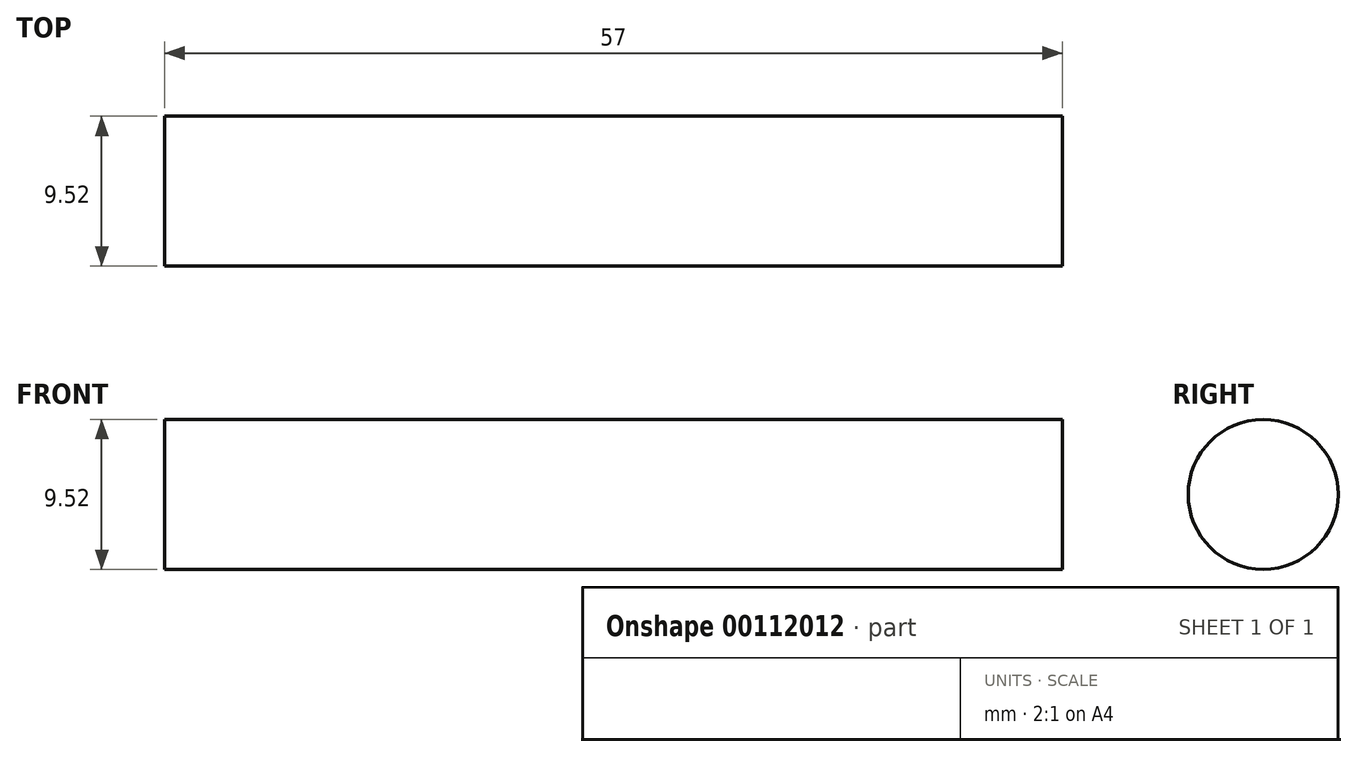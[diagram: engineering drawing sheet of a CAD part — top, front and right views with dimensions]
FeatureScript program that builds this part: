
annotation { "Feature Type Name" : "Feature", "Feature Type Description" : "" }
export const myFeature = defineFeature(function(context is Context, id is Id, definition is map)
    precondition{}
    {
        {
            var Q0;
            Q0=qCreatedBy(makeId("Right.planeOp"),FACE);
            var sketch = newSketch(context, id + "F0", { "sketchPlane" : qUnion([Q0])});
            skCircle(sketch, "E0", {"center": v(0, 0) * mm, "radius": 4.76 * mm});
            skSolve(sketch);
        }
        {
            var Q0;
            Q0 = qSketchRegion(id + "F0", true);
            extrude(context, id + "F1", {"entities" : qUnion([Q0]), "depth" : 57 * mm});
        }
    });
